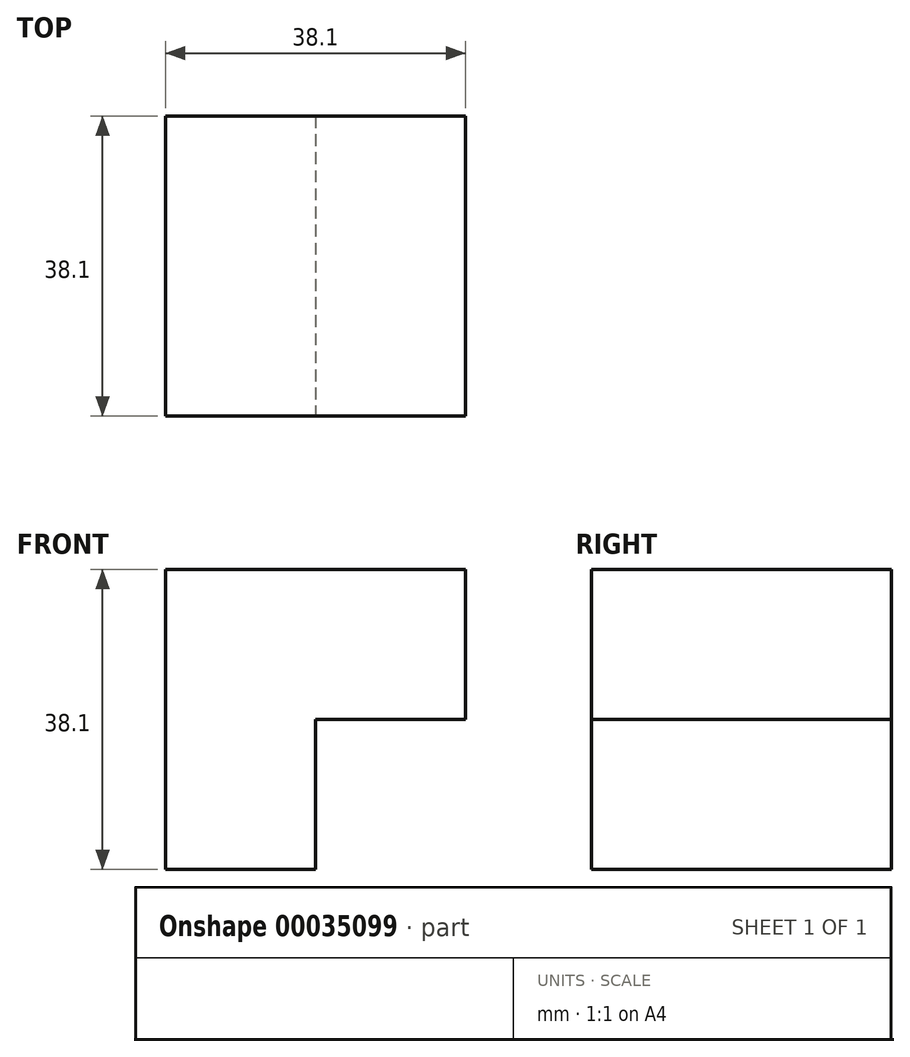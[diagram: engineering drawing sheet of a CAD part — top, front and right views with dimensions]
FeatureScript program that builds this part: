
annotation { "Feature Type Name" : "Feature", "Feature Type Description" : "" }
export const myFeature = defineFeature(function(context is Context, id is Id, definition is map)
    precondition{}
    {
        {
            var Q0;
            Q0=qCreatedBy(makeId("Top.planeOp"),FACE);
            var sketch = newSketch(context, id + "F0", { "sketchPlane" : qUnion([Q0])});
            skLineSegment(sketch, "E0.bottom", {"start": v(0, 0) * mm, "end": v(19.05, 0) * mm});
            skLineSegment(sketch, "E0.top", {"start": v(0, 19.05) * mm, "end": v(19.05, 19.05) * mm});
            skLineSegment(sketch, "E0.left", {"start": v(0, 0) * mm, "end": v(0, 19.05) * mm});
            skLineSegment(sketch, "E0.right", {"start": v(19.05, 0) * mm, "end": v(19.05, 19.05) * mm});
            skSolve(sketch);
        }
        {
            var Q0;
            Q0=makeQuery(id+"F0.imprint","IMPRINT",FACE,{"disambiguationData":[TD([[makeQuery(id+"F0.imprint","IMPRINT",EDGE,{"derivedFrom":sQuery(id+"F0.wireOp",EDGE,"E0.bottom")}),1.0]])]});
            extrude(context, id + "F1", {"entities" : qUnion([Q0]), "depth" : 19.05 * mm});
        }
        {
            var Q0;
            Q0=makeQuery(id+"F1.opExtrude","SWEPT_FACE",FACE,{"disambiguationData":[OSD([sQuery(id+"F0.wireOp",EDGE,"E0.top")])]});
            extrude(context, id + "F2", {"entities" : qUnion([Q0]), "operationType" : NewBodyOperationType.ADD, "depth" : 19.05 * mm});
        }
        {
            var Q0;
            {var subQ0=sQuery(id+"F0.wireOp",EDGE,"E0.top");Q0=makeQuery(id+"F2.boolean.opBoolean","MERGE",FACE,{"derivedFrom":[makeQuery(id+"F1.opExtrude","CAP_FACE",FACE,{"disambiguationData":[OSD([sQuery(id+"F0.wireOp",EDGE,"E0.bottom"),subQ0,sQuery(id+"F0.wireOp",EDGE,"E0.left"),sQuery(id+"F0.wireOp",EDGE,"E0.right")])],"isStart":false}),makeQuery(id+"F2.opExtrude","SWEPT_FACE",FACE,{"disambiguationData":[OSD([subQ0]),TDD([makeQuery(id+"F1.opExtrude","CAP_EDGE",EDGE,{"disambiguationData":[OSD([subQ0])],"isStart":false})])]})]});}
            extrude(context, id + "F3", {"entities" : qUnion([Q0]), "operationType" : NewBodyOperationType.ADD, "depth" : 19.05 * mm});
        }
        {
            var Q0;
            {var subQ0=sQuery(id+"F0.wireOp",EDGE,"E0.right");var subQ1=sQuery(id+"F0.wireOp",EDGE,"E0.top");Q0=makeQuery(id+"F3.boolean.opBoolean","MERGE",FACE,{"derivedFrom":[makeQuery(id+"F2.boolean.opBoolean","MERGE",FACE,{"derivedFrom":[makeQuery(id+"F1.opExtrude","SWEPT_FACE",FACE,{"disambiguationData":[OSD([subQ0])]}),makeQuery(id+"F2.opExtrude","SWEPT_FACE",FACE,{"disambiguationData":[OSD([subQ1,subQ0])]})]}),makeQuery(id+"F3.opExtrude","SWEPT_FACE",FACE,{"disambiguationData":[OSD([subQ1,subQ0])]})]});}
            var sketch = newSketch(context, id + "F4", { "sketchPlane" : qUnion([Q0])});
            skLineSegment(sketch, "E1.bottom", {"start": v(38.1, 38.1) * mm, "end": v(0, 38.1) * mm});
            skLineSegment(sketch, "E1.top", {"start": v(38.1, 19.05) * mm, "end": v(0, 19.05) * mm});
            skLineSegment(sketch, "E1.left", {"start": v(38.1, 38.1) * mm, "end": v(38.1, 19.05) * mm});
            skLineSegment(sketch, "E1.right", {"start": v(0, 38.1) * mm, "end": v(0, 19.05) * mm});
            skSolve(sketch);
        }
        {
            var Q0;
            Q0=makeQuery(id+"F4.imprint","IMPRINT",FACE,{"disambiguationData":[TD([[makeQuery(id+"F4.imprint","IMPRINT",EDGE,{"derivedFrom":sQuery(id+"F4.wireOp",EDGE,"E1.bottom")}),-1.0]])]});
            extrude(context, id + "F5", {"entities" : qUnion([Q0]), "operationType" : NewBodyOperationType.ADD, "depth" : 19.05 * mm});
        }
    });
